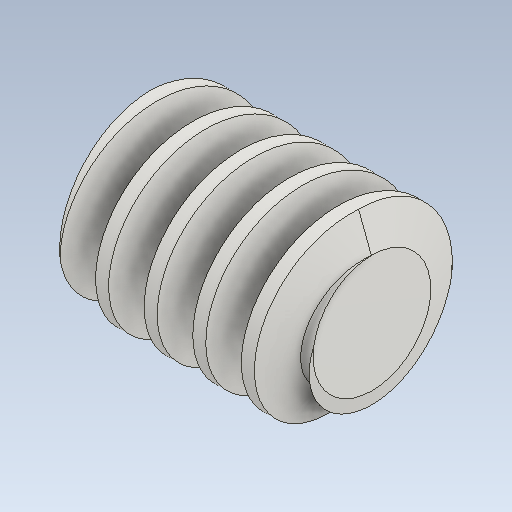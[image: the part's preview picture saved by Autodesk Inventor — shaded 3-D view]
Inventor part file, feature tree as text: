
AUTODESK INVENTOR PART (.ipt)
format: ipt  version: 2021 (Build 250183000, 183)  size: 310,272 bytes
history: native  units: mm (DEFAULTED — no unit token found)
features: other x6, chamfer x2, pattern_circular x2, extrude x1, sketch x1
ambient origin geometry x6: Origin, XZ Plane, X Axis, Y Axis, Z Axis, Center Point
bodies: Solid1 (feature_tree)
feature tree (12):
  extrude  "Base Body"  Depth=10.0mm
  chamfer  "Chamfer1"  Distance=60.0mm
  chamfer  "Chamfer2"  [1 undecoded]
  other  "Tooth Sketch"
  other  "Tooth"
  pattern_circular  "Tooth Pattern"  [2 undecoded]
  other  "Left Tooth"
  pattern_circular  "Left Tooth Pattern"  [2 undecoded]
  other  "Base Body Sketch"
  sketch  "Sketch5"  dims[d4=40.0mm d5=48.0mm d6=60.0mm d7=0.0mm d8=3.202938mm d9=8.8mm d10=3.202938mm d11=8.8mm d12=19.198622mm d14=3.1425mm d24=19.198622mm d25=43.982297mm d26=3.141593mm d27=15.2mm d28=20.0mm d29=24.24mm d30=12.566371mm d31=10.0mm d32=70.0mm d33=0.0mm d34=90.0deg d35=90.0deg d36=0.0mm d37=0.0mm d44=10.0mm d46=360.0deg d47=45.0deg d48=45.0deg d49=44.0mm d50=0.0mm d54=0.0mm d56=0.0mm d59=40.0mm d60=10.0mm d61=0.0mm d62=12.566371mm d63=10.0mm d64=70.0mm d65=0.0mm d66=90.0deg d67=90.0deg d68=0.0mm d69=0.0mm d70=10.0mm d71=10.0mm d72=10.0mm d73=360.0deg d75=10.0mm d76=10.0mm d77=0.0mm d79=44.0mm d80=0.0mm]
  other  "Srf1"
  other  "Pitch Diameter"
note: 5 required parameter values undecoded (feature->parameter linkage not recoverable at this tier; creation-order binding heuristic only, values carry confidence <= 0.55)
